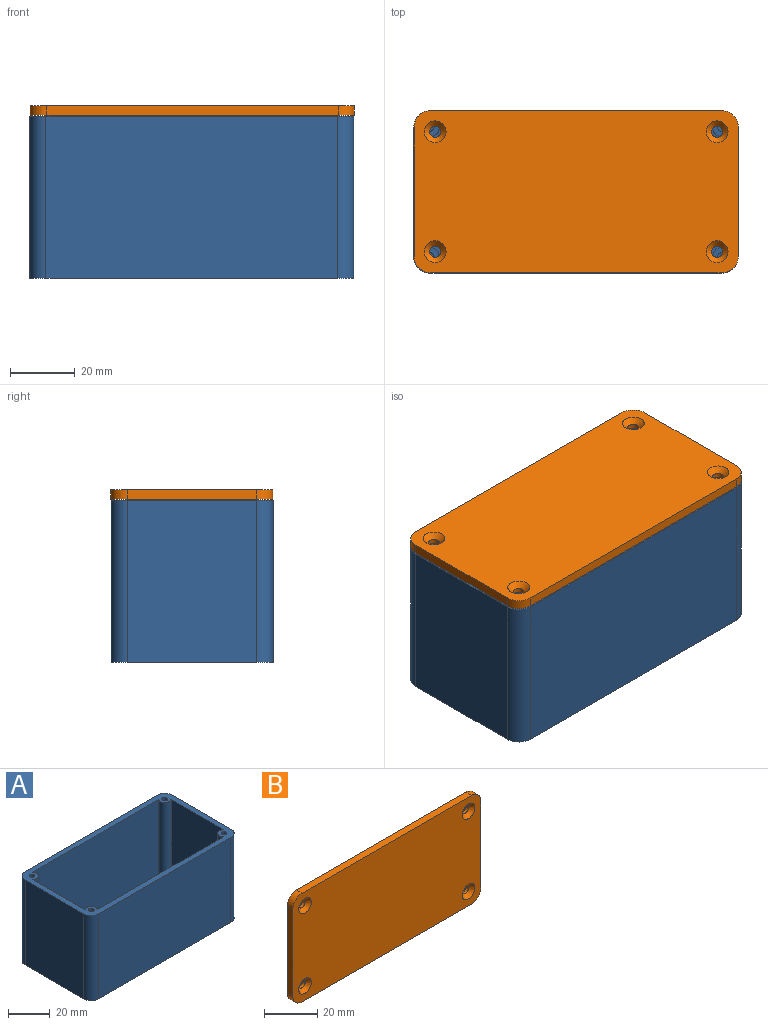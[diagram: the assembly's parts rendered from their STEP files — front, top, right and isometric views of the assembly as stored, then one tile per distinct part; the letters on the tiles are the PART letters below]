
ASSEMBLY  parts=2 mates=1
PART A: 27 faces, bbox 100x50x50 mm
  f0: plane 94x44mm, normal (0,0,1), area 4050.6mm2, adj f1,f2,f3,f4,f15,f18,f21,f24
  f1: plane 85.61x47mm, normal (0,-1,0), area 4023.6mm2, adj f0,f9,f15,f24
  f2: plane 47x35.5mm, normal (-1,0,0), area 1668.4mm2, adj f0,f9,f21,f24
  f3: plane 85.61x47mm, normal (0,1,0), area 4023.6mm2, adj f0,f9,f18,f21
  f4: plane 47x35.5mm, normal (1,0,0), area 1668.4mm2, adj f0,f9,f15,f18
  f5: plane 50x40mm, normal (1,0,0), area 2000mm2, adj f9,f10,f11,f14
  f6: plane 90x50mm, normal (0,1,0), area 4500mm2, adj f9,f10,f11,f12
  f7: plane 50x40mm, normal (-1,0,0), area 2000mm2, adj f9,f10,f12,f13
  f8: plane 90x50mm, normal (0,-1,0), area 4500mm2, adj f9,f10,f13,f14
  f9: plane 100x50mm, normal (0,0,1), area 904.1mm2, adj f1,f2,f3,f4,f5,f6,f7,f8
  f10: plane 100x50mm, normal (0,0,-1), area 4978.5mm2, adj f5,f6,f7,f8,f11,f12,f13,f14
  f11: cylinder r=5mm len=50mm, axis (0,0,1), area 392.7mm2, adj f5,f6,f9,f10
  f12: cylinder r=5mm len=50mm, axis (0,0,-1), area 392.7mm2, adj f6,f7,f9,f10
  f13: cylinder r=5mm len=50mm, axis (0,0,1), area 392.7mm2, adj f7,f8,f9,f10
  f14: cylinder r=5mm len=50mm, axis (0,0,-1), area 392.7mm2, adj f5,f8,f9,f10
  f15: cylinder r=3mm len=47mm, axis (0,0,-1), area 416mm2, adj f0,f1,f4,f9
  f16: cylinder r=1.38mm len=47mm, axis (0,0,-1), area 406.1mm2, adj f9,f17
  f17: plane 2.75x2.75mm, normal (0,0,1), area 5.9mm2, adj f16
  f18: cylinder r=3mm len=47mm, axis (0,0,-1), area 416mm2, adj f0,f3,f4,f9
  f19: cylinder r=1.38mm len=47mm, axis (0,0,-1), area 406.1mm2, adj f9,f20
  f20: plane 2.75x2.75mm, normal (0,0,1), area 5.9mm2, adj f19
  f21: cylinder r=3mm len=47mm, axis (0,0,-1), area 416mm2, adj f0,f2,f3,f9
  f22: cylinder r=1.38mm len=47mm, axis (0,0,-1), area 406.1mm2, adj f9,f23
  f23: plane 2.75x2.75mm, normal (0,0,1), area 5.9mm2, adj f22
  f24: cylinder r=3mm len=47mm, axis (0,0,-1), area 416mm2, adj f0,f1,f2,f9
  f25: cylinder r=1.38mm len=47mm, axis (0,0,-1), area 406.1mm2, adj f9,f26
  f26: plane 2.75x2.75mm, normal (0,0,1), area 5.9mm2, adj f25
PART B: 18 faces, bbox 100x3x50 mm
  f0: plane 40x3mm, normal (1,0,0), area 120mm2, adj f4,f5,f6,f9
  f1: plane 90x3mm, normal (0,0,1), area 270mm2, adj f4,f5,f6,f7
  f2: plane 40x3mm, normal (-1,0,0), area 120mm2, adj f4,f5,f7,f8
  f3: plane 90x3mm, normal (0,0,-1), area 270mm2, adj f4,f5,f8,f9
  f4: plane 100x50mm, normal (0,-1,0), area 4836.7mm2, adj f0,f1,f2,f3,f6,f7,f8,f9
  f5: plane 100x50mm, normal (0,1,0), area 4942.2mm2, adj f0,f1,f2,f3,f6,f7,f8,f9
  f6: cylinder r=5mm len=5mm, axis (0,-1,0), area 23.6mm2, adj f0,f1,f4,f5
  f7: cylinder r=5mm len=5mm, axis (0,1,0), area 23.6mm2, adj f1,f2,f4,f5
  f8: cylinder r=5mm len=5mm, axis (0,-1,0), area 23.6mm2, adj f2,f3,f4,f5
  f9: cylinder r=5mm len=5mm, axis (0,1,0), area 23.6mm2, adj f0,f3,f4,f5
  f10: cylinder r=1.7mm len=3.4mm, axis (0,-1,0), area 14.3mm2, adj f5,f11
  f11: cone r=1.7mm half-angle=45deg, axis (0,-1,0), area 37.3mm2, adj f4,f10
  f12: cylinder r=1.7mm len=3.4mm, axis (0,-1,0), area 14.3mm2, adj f5,f13
  f13: cone r=1.7mm half-angle=45deg, axis (0,-1,0), area 37.3mm2, adj f4,f12
  f14: cylinder r=1.7mm len=3.4mm, axis (0,-1,0), area 14.3mm2, adj f5,f15
  f15: cone r=1.7mm half-angle=45deg, axis (0,-1,0), area 37.3mm2, adj f4,f14
  f16: cylinder r=1.7mm len=3.4mm, axis (0,-1,0), area 14.3mm2, adj f5,f17
  f17: cone r=1.7mm half-angle=45deg, axis (0,-1,0), area 37.3mm2, adj f4,f16
PLACE A rot(axis=(0.98,0.16,-0.08),0deg) t=(4.78,-22.36,-35.76)mm
PLACE B rot(axis=(-1,0,0),90deg) t=(4.89,-22.29,14.56)mm
MATE slider A.f24 <-> B.f6  axis (0,0,1) through (49.89,-2.29,14.24)mm
